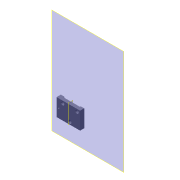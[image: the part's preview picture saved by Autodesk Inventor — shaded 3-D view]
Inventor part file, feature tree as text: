
AUTODESK INVENTOR PART (.ipt)
format: ipt  version: 2022 (Build 260153000, 153)  size: 113,664 bytes
history: native  units: mm
features: extrude x3, sketch x3, other x2, plane x1, projected_geometry x1
ambient origin geometry x8: Origin, YZ Plane, XZ Plane, XY Plane, X Axis, Y Axis, Z Axis, Center Point
bodies: Solid1 (feature_tree)
feature tree (10):
  plane  "Work Plane1"
  extrude  "Extrusion1"  Depth=5.9mm
  extrude  "Extrusion2"  Depth=4.0mm TaperAngle=0.0deg
  extrude  "Extrusion5"  Depth=1.5mm
  sketch  "Sketch1"  dims[d4=5.9mm d5=5.9mm]
  sketch  "Sketch2"  dims[d6=5.9mm d7=4.0mm d8=0.0mm]
  projected_geometry  "Projected Loop1"
  sketch  "Sketch5"  dims[d11=1.5mm d12=0.0mm d30=2.8mm d31=2.8mm d32=0.0mm d37=12.124356mm d38=12.124356mm]
  other  "cellSTORM_v5.iam"
  other  "cellSTORM_Base_v0_R1:1"
